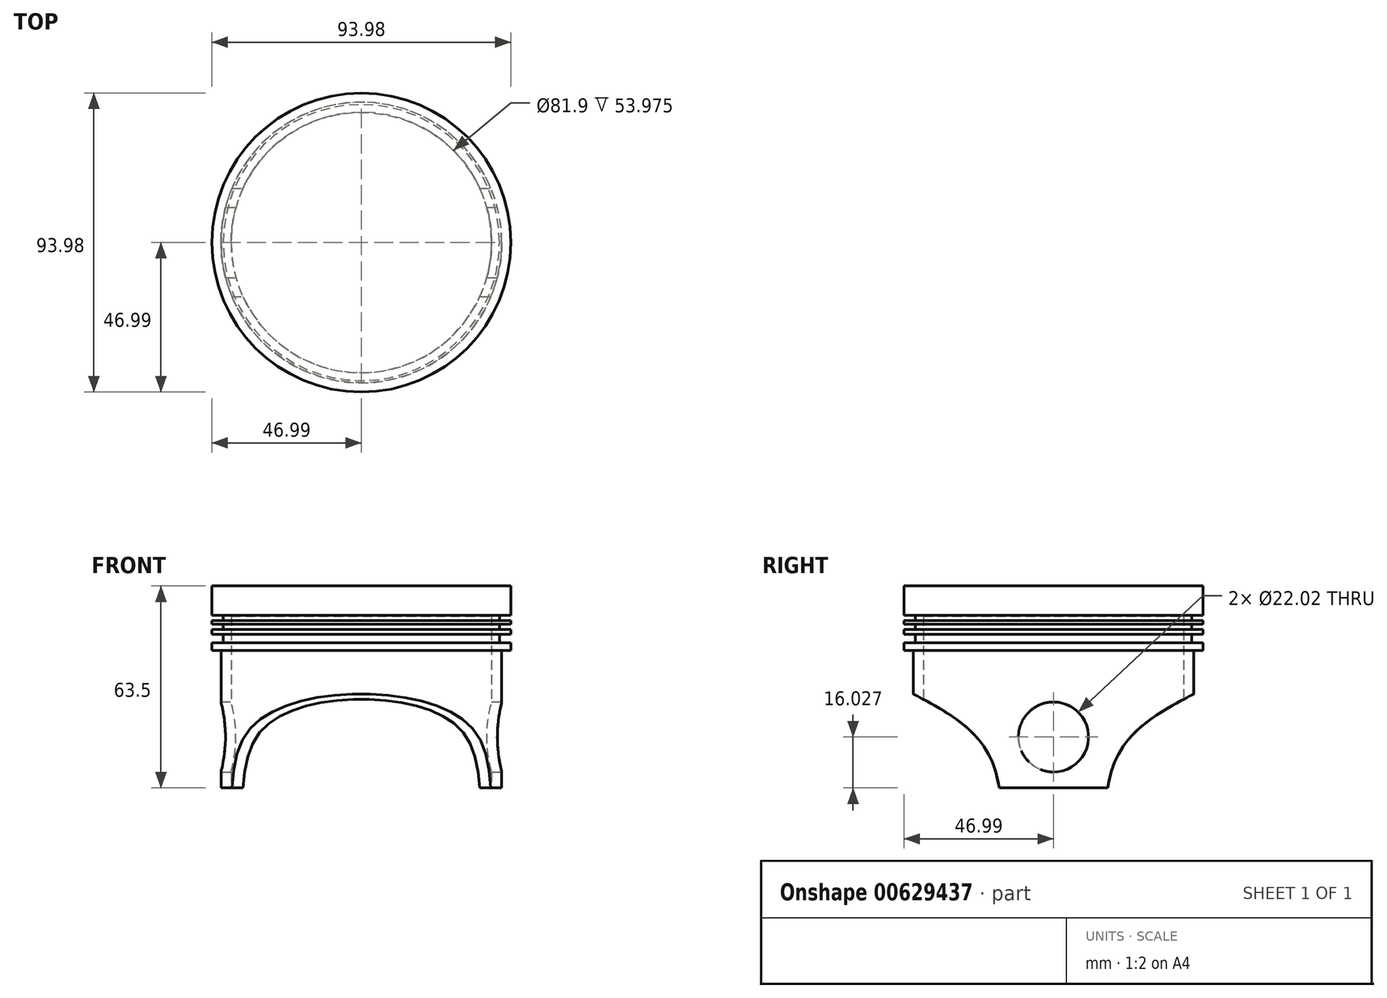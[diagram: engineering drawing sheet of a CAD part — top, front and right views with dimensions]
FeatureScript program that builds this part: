
annotation { "Feature Type Name" : "Feature", "Feature Type Description" : "" }
export const myFeature = defineFeature(function(context is Context, id is Id, definition is map)
    precondition{}
    {
        {
            var Q0;
            Q0=qCreatedBy(makeId("Top.planeOp"),FACE);
            var sketch = newSketch(context, id + "F0", { "sketchPlane" : qUnion([Q0])});
            skCircle(sketch, "E0", {"center": v(0, 0) * mm, "radius": 47 * mm});
            skSolve(sketch);
        }
        {
            var Q0;
            Q0=makeQuery(id+"F0.imprint","IMPRINT",FACE,{"disambiguationData":[TD([[makeQuery(id+"F0.imprint","IMPRINT",EDGE,{"derivedFrom":sQuery(id+"F0.wireOp",EDGE,"E0")}),1.0]])]});
            extrude(context, id + "F1", {"entities" : qUnion([Q0]), "depth" : 63.5 * mm, "offsetDistance" : 25.4 * mm});
        }
        {
            var Q0;
            Q0=qCreatedBy(makeId("Right.planeOp"),FACE);
            var sketch = newSketch(context, id + "F2", { "sketchPlane" : qUnion([Q0])});
            skLineSegment(sketch, "E1.bottom", {"start": v(-52.98, 0) * mm, "end": v(-44.12, 0) * mm});
            skLineSegment(sketch, "E1.top", {"start": v(-52.98, 43.2) * mm, "end": v(-44.12, 43.2) * mm});
            skLineSegment(sketch, "E1.left", {"start": v(-52.98, 0) * mm, "end": v(-52.98, 43.2) * mm});
            skLineSegment(sketch, "E1.right", {"start": v(-44.12, 0) * mm, "end": v(-44.12, 43.2) * mm});
            skSolve(sketch);
        }
        {
            var Q0;
            Q0=makeQuery(id+"F2.imprint","IMPRINT",FACE,{"disambiguationData":[TD([[makeQuery(id+"F2.imprint","IMPRINT",EDGE,{"derivedFrom":sQuery(id+"F2.wireOp",EDGE,"E1.bottom")}),1.0]])]});
            var Q1;
            Q1=makeQuery(id+"F1.opExtrude","CAP_EDGE",EDGE,{"disambiguationData":[OSD([sQuery(id+"F0.wireOp",EDGE,"E0")])],"isStart":true});
            revolve(context, id + "F3", {"operationType" : NewBodyOperationType.REMOVE, "entities" : qUnion([Q0]), "axis" : qUnion([Q1]), "revolveType" : RevolveType.FULL, "oppositeDirection" : true});
        }
        {
            var Q0;
            Q0=qCreatedBy(makeId("Right.planeOp"),FACE);
            var sketch = newSketch(context, id + "F4", { "sketchPlane" : qUnion([Q0])});
            skLineSegment(sketch, "E2.bottom", {"start": v(-48.84, 54.3) * mm, "end": v(-43.4, 54.3) * mm});
            skLineSegment(sketch, "E2.top", {"start": v(-48.84, 52.65) * mm, "end": v(-43.4, 52.65) * mm});
            skLineSegment(sketch, "E2.left", {"start": v(-48.84, 54.3) * mm, "end": v(-48.84, 52.65) * mm});
            skLineSegment(sketch, "E2.right", {"start": v(-43.4, 54.3) * mm, "end": v(-43.4, 52.65) * mm});
            skLineSegment(sketch, "E3.bottom", {"start": v(-48.84, 51.54) * mm, "end": v(-43.4, 51.54) * mm});
            skLineSegment(sketch, "E3.top", {"start": v(-48.84, 49.84) * mm, "end": v(-43.4, 49.84) * mm});
            skLineSegment(sketch, "E3.left", {"start": v(-48.84, 51.54) * mm, "end": v(-48.84, 49.84) * mm});
            skLineSegment(sketch, "E3.right", {"start": v(-43.4, 51.54) * mm, "end": v(-43.4, 49.84) * mm});
            skLineSegment(sketch, "E4.bottom", {"start": v(-48.84, 48.31) * mm, "end": v(-43.4, 48.31) * mm});
            skLineSegment(sketch, "E4.top", {"start": v(-48.84, 45.62) * mm, "end": v(-43.4, 45.62) * mm});
            skLineSegment(sketch, "E4.left", {"start": v(-48.84, 48.31) * mm, "end": v(-48.84, 45.62) * mm});
            skLineSegment(sketch, "E4.right", {"start": v(-43.4, 48.31) * mm, "end": v(-43.4, 45.62) * mm});
            skSolve(sketch);
        }
        {
            var Q0;
            Q0 = qSketchRegion(id + "F4", true);
            var Q1;
            Q1=makeQuery(id+"F3.boolean.opBoolean","INTERSECT",EDGE,{"derivedFrom":[makeQuery(id+"F1.opExtrude","SWEPT_FACE",FACE,{"disambiguationData":[OSD([sQuery(id+"F0.wireOp",EDGE,"E0")])]}),makeQuery(id+"F3.opRevolve","SWEPT_FACE",FACE,{"disambiguationData":[OSD([sQuery(id+"F2.wireOp",EDGE,"E1.top")])]})]});
            revolve(context, id + "F5", {"operationType" : NewBodyOperationType.REMOVE, "entities" : qUnion([Q0]), "axis" : qUnion([Q1]), "revolveType" : RevolveType.FULL, "oppositeDirection" : true});
        }
        {
            var Q0;
            Q0=makeQuery(id+"F1.opExtrude","CAP_FACE",FACE,{"disambiguationData":[OSD([sQuery(id+"F0.wireOp",EDGE,"E0")])],"isStart":true});
            var sketch = newSketch(context, id + "F6", { "sketchPlane" : qUnion([Q0])});
            skCircle(sketch, "E5.0", {"center": v(0, 0) * mm, "radius": 40.95 * mm});
            skSolve(sketch);
        }
        {
            var Q0;
            Q0=makeQuery(id+"F6.imprint","IMPRINT",FACE,{"disambiguationData":[TD([[makeQuery(id+"F6.imprint","IMPRINT",EDGE,{"derivedFrom":sQuery(id+"F6.wireOp",EDGE,"E5.0")}),1.0]])]});
            extrude(context, id + "F7", {"entities" : qUnion([Q0]), "operationType" : NewBodyOperationType.REMOVE, "oppositeDirection" : true, "depth" : 53.97 * mm, "offsetDistance" : 25.4 * mm});
        }
        {
            var Q0;
            Q0=qCreatedBy(makeId("Right.planeOp"),FACE);
            var sketch = newSketch(context, id + "F8", { "sketchPlane" : qUnion([Q0])});
            skFitSpline(sketch, "E6", {"points": [v(-46.97, 31.08) * mm, v(-28.02, 19.65) * mm, v(-18.54, 6.27) * mm, v(-16.03, -11.85) * mm, v(-15.75, -20.5) * mm], "startDerivative": vector(70.14, -36.39) * mm, "endDerivative": vector(1.09, -41.65) * mm});
            skLineSegment(sketch, "E7", {"start": v(-15.75, -20.5) * mm, "end": v(-50.6, -20.5) * mm});
            skLineSegment(sketch, "E8", {"start": v(-50.6, -20.5) * mm, "end": v(-46.97, 31.08) * mm});
            skCircle(sketch, "E9", {"center": v(0, 16.03) * mm, "radius": 11.01 * mm});
            skFitSpline(sketch, "E10.MirrorCS", {"points": [v(46.97, 31.08) * mm, v(28.02, 19.65) * mm, v(18.54, 6.27) * mm, v(16.03, -11.85) * mm, v(15.75, -20.5) * mm], "startDerivative": vector(-70.14, -36.39) * mm, "endDerivative": vector(-1.09, -41.65) * mm});
            skLineSegment(sketch, "E11.MirrorCS", {"start": v(15.75, -20.5) * mm, "end": v(50.6, -20.5) * mm});
            skLineSegment(sketch, "E12.MirrorCS", {"start": v(50.6, -20.5) * mm, "end": v(46.97, 31.08) * mm});
            skSolve(sketch);
        }
        {
            var Q0;
            Q0=makeQuery(id+"F8.imprint","IMPRINT",FACE,{"disambiguationData":[TD([[makeQuery(id+"F8.imprint","IMPRINT",EDGE,{"derivedFrom":sQuery(id+"F8.wireOp",EDGE,"E6")}),-1.0]])]});
            var Q1;
            Q1=makeQuery(id+"F8.imprint","IMPRINT",FACE,{"disambiguationData":[TD([[makeQuery(id+"F8.imprint","IMPRINT",EDGE,{"derivedFrom":sQuery(id+"F8.wireOp",EDGE,"E9")}),1.0]])]});
            var Q2;
            Q2=makeQuery(id+"F8.imprint","IMPRINT",FACE,{"disambiguationData":[TD([[makeQuery(id+"F8.imprint","IMPRINT",EDGE,{"derivedFrom":sQuery(id+"F8.wireOp",EDGE,"E10.MirrorCS")}),1.0]])]});
            extrude(context, id + "F9", {"entities" : qUnion([Q0, Q1, Q2]), "operationType" : NewBodyOperationType.REMOVE, "oppositeDirection" : true, "depth" : 101.6 * mm, "offsetDistance" : 25.4 * mm, "symmetric" : true});
        }
    });
